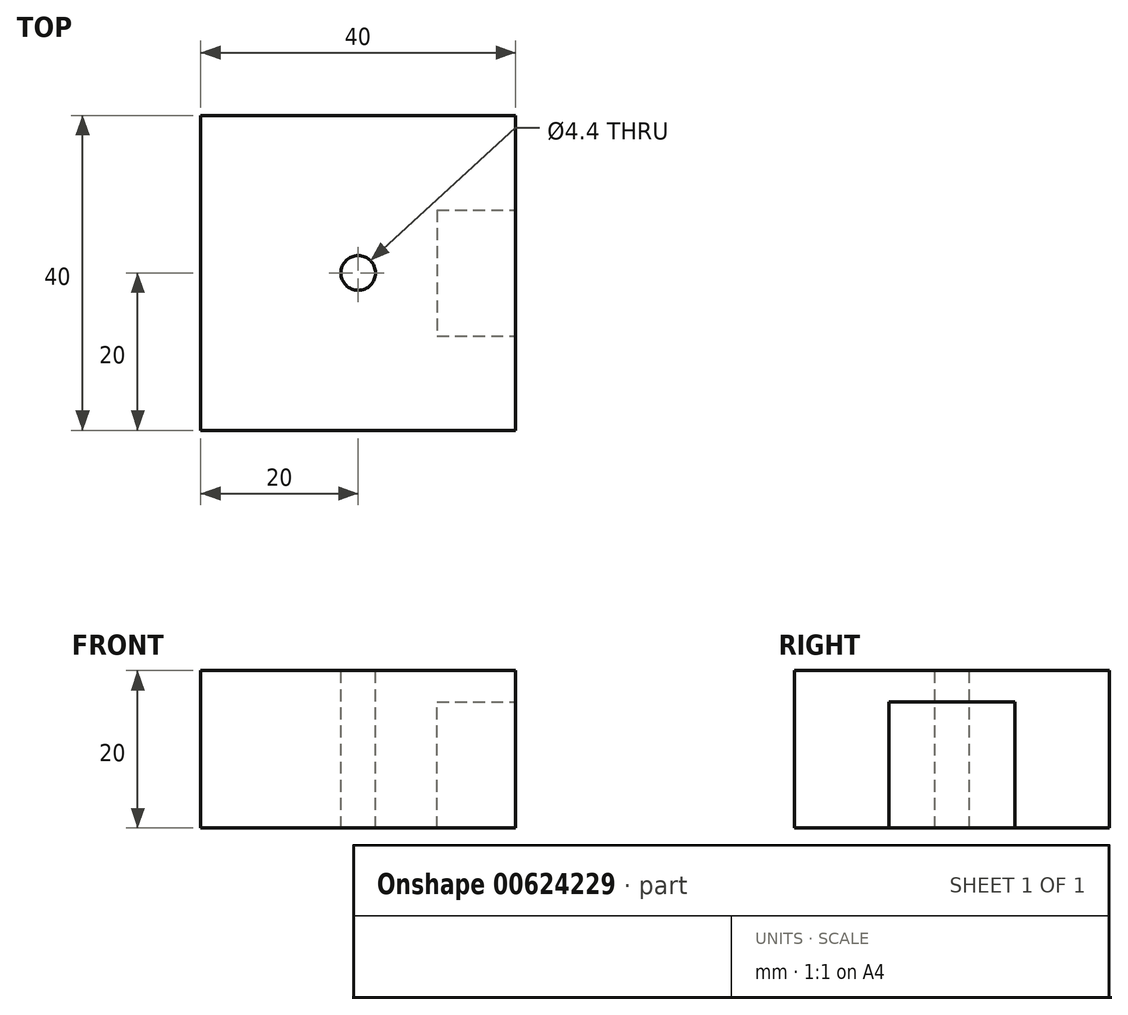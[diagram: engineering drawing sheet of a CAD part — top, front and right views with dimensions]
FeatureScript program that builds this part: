
annotation { "Feature Type Name" : "Feature", "Feature Type Description" : "" }
export const myFeature = defineFeature(function(context is Context, id is Id, definition is map)
    precondition{}
    {
        {
            var Q0;
            Q0=qCreatedBy(makeId("Top.planeOp"),FACE);
            var sketch = newSketch(context, id + "F0", { "sketchPlane" : qUnion([Q0])});
            skLineSegment(sketch, "E0.bottom", {"start": v(-20, 20) * mm, "end": v(20, 20) * mm});
            skLineSegment(sketch, "E0.top", {"start": v(-20, -20) * mm, "end": v(20, -20) * mm});
            skLineSegment(sketch, "E0.left", {"start": v(-20, 20) * mm, "end": v(-20, -20) * mm});
            skLineSegment(sketch, "E0.right", {"start": v(20, 20) * mm, "end": v(20, -20) * mm});
            skSolve(sketch);
        }
        {
            var Q0;
            Q0=makeQuery(id+"F0.imprint","IMPRINT",FACE,{"disambiguationData":[TD([[makeQuery(id+"F0.imprint","IMPRINT",EDGE,{"derivedFrom":sQuery(id+"F0.wireOp",EDGE,"E0.bottom")}),-1.0]])]});
            extrude(context, id + "F1", {"entities" : qUnion([Q0]), "depth" : 20 * mm, "offsetDistance" : 25 * mm});
        }
        {
            var Q0;
            Q0=makeQuery(id+"F1.opExtrude","SWEPT_FACE",FACE,{"disambiguationData":[OSD([sQuery(id+"F0.wireOp",EDGE,"E0.right")])]});
            var sketch = newSketch(context, id + "F2", { "sketchPlane" : qUnion([Q0])});
            skLineSegment(sketch, "E1.bottom", {"start": v(-8, 0) * mm, "end": v(8, 0) * mm});
            skLineSegment(sketch, "E1.top", {"start": v(-8, 16) * mm, "end": v(8, 16) * mm});
            skLineSegment(sketch, "E1.left", {"start": v(-8, 0) * mm, "end": v(-8, 16) * mm});
            skLineSegment(sketch, "E1.right", {"start": v(8, 0) * mm, "end": v(8, 16) * mm});
            skSolve(sketch);
        }
        {
            var Q0;
            Q0=makeQuery(id+"F2.imprint","IMPRINT",FACE,{"disambiguationData":[TD([[makeQuery(id+"F2.imprint","IMPRINT",EDGE,{"derivedFrom":sQuery(id+"F2.wireOp",EDGE,"E1.bottom")}),-1.0]])]});
            extrude(context, id + "F3", {"entities" : qUnion([Q0]), "operationType" : NewBodyOperationType.REMOVE, "oppositeDirection" : true, "depth" : 10 * mm, "offsetDistance" : 25 * mm});
        }
        {
            var Q0;
            Q0=makeQuery(id+"F1.opExtrude","CAP_FACE",FACE,{"disambiguationData":[OSD([sQuery(id+"F0.wireOp",EDGE,"E0.bottom"),sQuery(id+"F0.wireOp",EDGE,"E0.top"),sQuery(id+"F0.wireOp",EDGE,"E0.left"),sQuery(id+"F0.wireOp",EDGE,"E0.right")])],"isStart":false});
            var sketch = newSketch(context, id + "F4", { "sketchPlane" : qUnion([Q0])});
            skPoint(sketch, "E2", {"position": v(0, 0) * mm});
            skSolve(sketch);
        }
        {
            var Q0;
            Q0=sQuery(id+"F4.wireOp",VERTEX,"E2");
            var Q1;
            Q1=makeQuery(id+"F1.opExtrude","SWEPT_BODY",BODY,{"disambiguationData":[OSD([sQuery(id+"F0.wireOp",EDGE,"E0.bottom"),sQuery(id+"F0.wireOp",EDGE,"E0.top"),sQuery(id+"F0.wireOp",EDGE,"E0.left"),sQuery(id+"F0.wireOp",EDGE,"E0.right")])]});
            hole(context, id + "F5", {"style" : HoleStyle.SIMPLE, "endStyle" : HoleEndStyle.THROUGH, "standardTappedOrClearance" : lookupTablePath({ "standard" : "ISO", "fit" : "Normal", "size" : "M4", "type" : "Clearance" }), "standardBlindInLast" : lookupTablePath({ "fit" : "Standard", "standard" : "ISO", "size" : "M4", "type" : "Clearance" }), "holeDiameter" : 4.4 * mm, "majorDiameter" : 5 * mm, "isTappedThrough" : true, "tappedDepth" : 12 * mm, "tapClearance" : 3, "locations" : qUnion([Q0]), "scope" : qUnion([Q1])});
        }
    });
